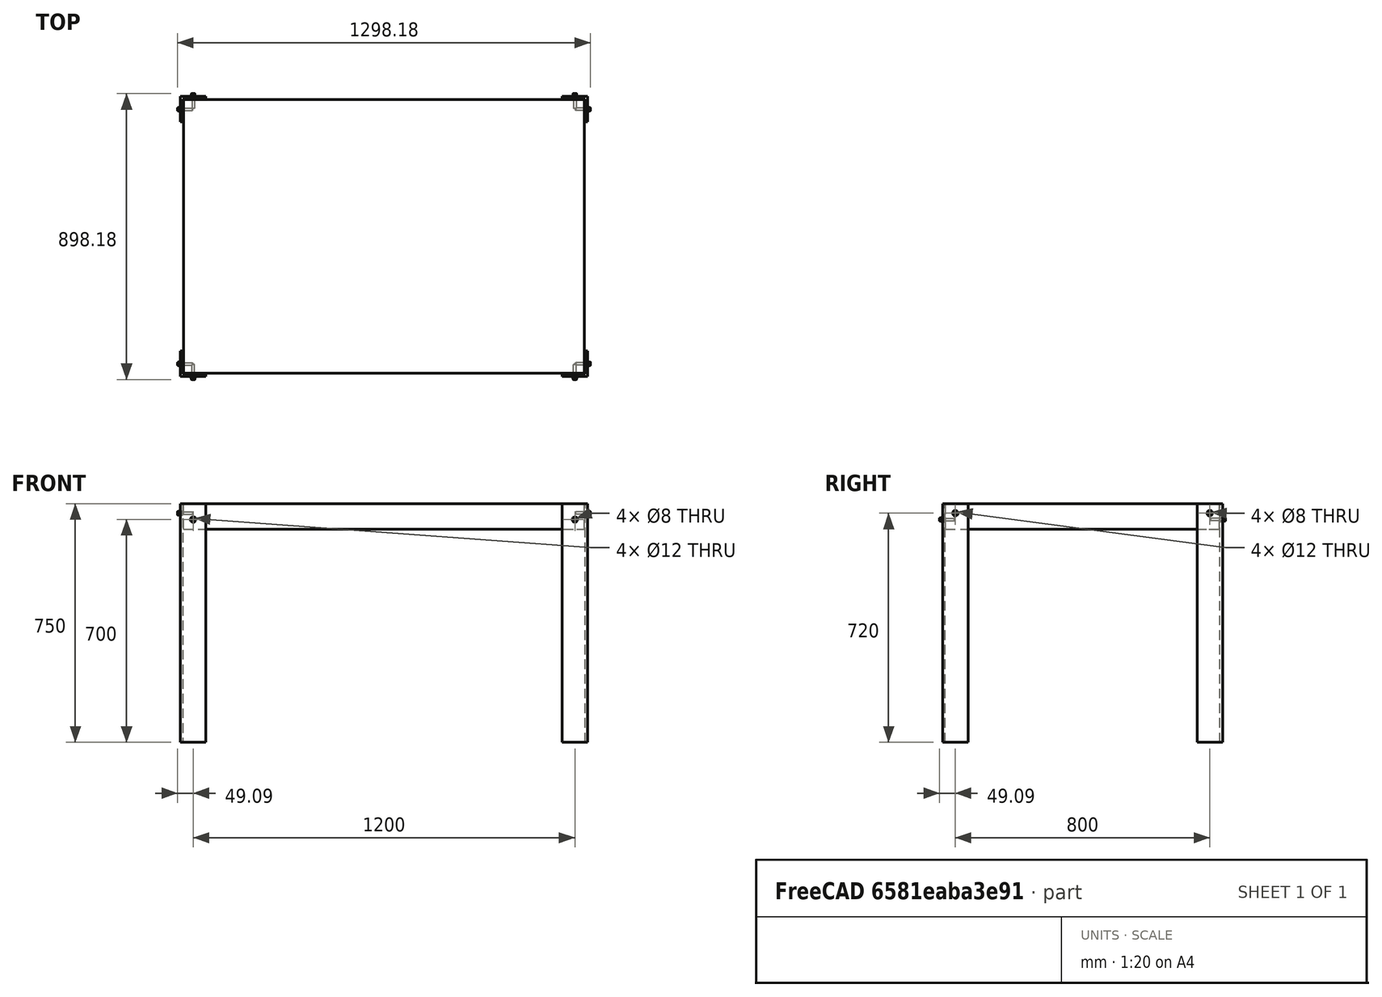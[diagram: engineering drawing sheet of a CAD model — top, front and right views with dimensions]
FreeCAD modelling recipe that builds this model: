
FCSTD DOCUMENT  (FreeCAD 0.17R7797 (Git))
Label: render
License: CreativeCommons Attribution
LicenseURL: http://creativecommons.org/licenses/by/4.0/
objects: Raytracing::RayFeature×13, Raytracing::LuxFeature×13, Part::Cut×12, Part::Box×9, Part::FeaturePython×8, Part::Cylinder×4, App::DocumentObjectGroup×1, Raytracing::RayProject×1, Raytracing::LuxProject×1
note: 33 computed .brp shape members not serialized (recipe doc carries the construction recipe); baked Part::Feature solids carry a one-line shape summary decoded from their .brp

FEATURE [Part::Box] Box  label="Cube"
  AttacherType = Attacher::AttachEngine3D
  Height = 750
  Length = 80
  Width = 80
FEATURE [Part::Box] Box001  label="Cube001"
  AttacherType = Attacher::AttachEngine3D
  Height = 750
  Length = 80
  Placement = pos=(8,8,0) rot=(0,0,1;0rad)
  Width = 80
FEATURE [Part::Cut] Cut
  Base = -> Box
  Tool = -> Box001
FEATURE [Part::Box] Box002  label="Cube002"
  AttacherType = Attacher::AttachEngine3D
  Height = 750
  Length = 80
  Placement = pos=(0,800,0) rot=(0,0,1;0rad)
  Width = 80
FEATURE [Part::Box] Box003  label="Cube003"
  AttacherType = Attacher::AttachEngine3D
  Height = 750
  Length = 80
  Placement = pos=(8,792,0) rot=(0,0,1;0rad)
  Width = 80
FEATURE [Part::Cut] Cut001
  Base = -> Box002
  Tool = -> Box003
FEATURE [Part::Box] Box004  label="Cube004"
  AttacherType = Attacher::AttachEngine3D
  Height = 750
  Length = 80
  Placement = pos=(1200,0,0) rot=(0,0,1;0rad)
  Width = 80
FEATURE [Part::Box] Box005  label="Cube005"
  AttacherType = Attacher::AttachEngine3D
  Height = 750
  Length = 80
  Placement = pos=(1192,8,0) rot=(0,0,1;0rad)
  Width = 80
FEATURE [Part::Cut] Cut002
  Base = -> Box004
  Tool = -> Box005
FEATURE [Part::Box] Box006  label="Cube006"
  AttacherType = Attacher::AttachEngine3D
  Height = 750
  Length = 80
  Placement = pos=(1200,800,0) rot=(0,0,1;0rad)
  Width = 80
FEATURE [Part::Box] Box007  label="Cube007"
  AttacherType = Attacher::AttachEngine3D
  Height = 750
  Length = 80
  Placement = pos=(1192,792,0) rot=(0,0,1;0rad)
  Width = 80
FEATURE [Part::Cut] Cut003
  Base = -> Box006
  Tool = -> Box007
FEATURE [Part::Box] Box008  label="Tabletop"
  AttacherType = Attacher::AttachEngine3D
  Height = 80
  Length = 1260
  Placement = pos=(10,10,670) rot=(0,0,1;0rad)
  Width = 860
  expr: Width = 880 - 20
  expr: Length = 1280 - 20
FEATURE [Part::Cylinder] Cylinder
  Angle = 360
  AttacherType = Attacher::AttachEngine3D
  Height = 1300
  Placement = pos=(-10,40,720) rot=(0,1,0;1.5708rad)
  Radius = 6
FEATURE [Part::Cylinder] Cylinder001
  Angle = 360
  AttacherType = Attacher::AttachEngine3D
  Height = 1300
  Placement = pos=(-10,840,720) rot=(0,1,0;1.5708rad)
  Radius = 6
FEATURE [Part::Cylinder] Cylinder002
  Angle = 360
  AttacherType = Attacher::AttachEngine3D
  Height = 900
  Placement = pos=(40,-10,700) rot=(-1,0,0;1.5708rad)
  Radius = 6
FEATURE [Part::Cylinder] Cylinder003
  Angle = 360
  AttacherType = Attacher::AttachEngine3D
  Height = 900
  Placement = pos=(1240,-10,700) rot=(-1,0,0;1.5708rad)
  Radius = 6
FEATURE [Part::Cut] Cut004
  Base = -> Cut
  Tool = -> Cylinder
FEATURE [Part::Cut] Cut005
  Base = -> Cut002
  Tool = -> Cylinder
FEATURE [Part::Cut] Cut006  label="Foot 01"
  Base = -> Cut004
  Tool = -> Cylinder002
FEATURE [Part::Cut] Cut007
  Base = -> Cut001
  Tool = -> Cylinder002
FEATURE [Part::Cut] Cut008  label="Foot 02"
  Base = -> Cut007
  Tool = -> Cylinder001
FEATURE [Part::Cut] Cut009
  Base = -> Cut003
  Tool = -> Cylinder001
FEATURE [Part::Cut] Cut010  label="Foot 03"
  Base = -> Cut009
  Tool = -> Cylinder003
FEATURE [Part::Cut] Cut011  label="Foot 04"
  Base = -> Cut005
  Tool = -> Cylinder003
FEATURE [Part::FeaturePython] Screw  label="M8x40-Screw"  # Fasteners workbench fastener (typed FeaturePython)
  Placement = pos=(-2,40,720) rot=(0,-1,0;1.5708rad)
  diameter = 3
  invert = false
  length = 5
  matchOuter = false
  offset = 0
  thread = false
  type = 1
FEATURE [Part::FeaturePython] Screw001  label="M8x40-Screw001"  # Fasteners workbench fastener (typed FeaturePython)
  Placement = pos=(-2,840,720) rot=(0,-1,0;1.5708rad)
  diameter = 3
  invert = false
  length = 5
  matchOuter = false
  offset = 0
  thread = false
  type = 1
FEATURE [Part::FeaturePython] Screw002  label="M8x40-Screw002"  # Fasteners workbench fastener (typed FeaturePython)
  Placement = pos=(1282,40,720) rot=(0,1,0;1.5708rad)
  diameter = 3
  invert = false
  length = 5
  matchOuter = false
  offset = 0
  thread = false
  type = 1
FEATURE [Part::FeaturePython] Screw003  label="M8x40-Screw003"  # Fasteners workbench fastener (typed FeaturePython)
  Placement = pos=(1282,840,720) rot=(0,1,0;1.5708rad)
  diameter = 3
  invert = false
  length = 5
  matchOuter = false
  offset = 0
  thread = false
  type = 1
FEATURE [Part::FeaturePython] Screw004  label="M8x40-Screw007"  # Fasteners workbench fastener (typed FeaturePython)
  Placement = pos=(40,882,700) rot=(-1,0,0;1.5708rad)
  diameter = 3
  invert = false
  length = 5
  matchOuter = false
  offset = 0
  thread = false
  type = 1
FEATURE [Part::FeaturePython] Screw005  label="M8x40-Screw005"  # Fasteners workbench fastener (typed FeaturePython)
  Placement = pos=(1240,-2,700) rot=(1,0,0;1.5708rad)
  diameter = 3
  invert = false
  length = 5
  matchOuter = false
  offset = 0
  thread = false
  type = 1
FEATURE [Part::FeaturePython] Screw006  label="M8x40-Screw006"  # Fasteners workbench fastener (typed FeaturePython)
  Placement = pos=(40,-2,700) rot=(1,0,0;1.5708rad)
  diameter = 3
  invert = false
  length = 5
  matchOuter = false
  offset = 0
  thread = false
  type = 1
FEATURE [Part::FeaturePython] Screw007  label="M8x40-Screw008"  # Fasteners workbench fastener (typed FeaturePython)
  Placement = pos=(1240,882,700) rot=(-1,0,0;1.5708rad)
  diameter = 3
  invert = false
  length = 5
  matchOuter = false
  offset = 0
  thread = false
  type = 1
FEATURE [App::DocumentObjectGroup] Group  label="Screws"
  Group = -> [Screw,Screw001,Screw002,Screw003,Screw004,Screw005,Screw006,Screw007]
FEATURE [Raytracing::RayFeature] Cut006_View
  Result = <blob: 18464 chars omitted>
  Source = -> Cut006
  Transparency = 0
FEATURE [Raytracing::RayFeature] Cut008_View
  Result = <blob: 18274 chars omitted>
  Source = -> Cut008
  Transparency = 0
FEATURE [Raytracing::RayFeature] Cut010_View
  Result = <blob: 18288 chars omitted>
  Source = -> Cut010
  Transparency = 0
FEATURE [Raytracing::RayFeature] Cut011_View
  Result = <blob: 18398 chars omitted>
  Source = -> Cut011
  Transparency = 0
FEATURE [Raytracing::RayFeature] Box008_View
  Result = <blob: 2757 chars omitted>
  Source = -> Box008
  Transparency = 0
FEATURE [Raytracing::RayFeature] Screw_View
  Result = <blob: 147194 chars omitted>
  Source = -> Screw
  Transparency = 0
FEATURE [Raytracing::RayFeature] Screw001_View
  Result = <blob: 147808 chars omitted>
  Source = -> Screw001
  Transparency = 0
FEATURE [Raytracing::RayFeature] Screw002_View
  Result = <blob: 146709 chars omitted>
  Source = -> Screw002
  Transparency = 0
FEATURE [Raytracing::RayFeature] Screw003_View
  Result = <blob: 147088 chars omitted>
  Source = -> Screw003
  Transparency = 0
FEATURE [Raytracing::RayFeature] Screw004_View
  Result = <blob: 147220 chars omitted>
  Source = -> Screw004
  Transparency = 0
FEATURE [Raytracing::RayFeature] Screw005_View
  Result = <blob: 148196 chars omitted>
  Source = -> Screw005
  Transparency = 0
FEATURE [Raytracing::RayFeature] Screw006_View
  Result = <blob: 148226 chars omitted>
  Source = -> Screw006
  Transparency = 0
FEATURE [Raytracing::RayFeature] Screw007_View
  Result = <blob: 147459 chars omitted>
  Source = -> Screw007
  Transparency = 0
FEATURE [Raytracing::RayProject] PovProject
  Camera = // declares positon and view direction\n\n// Generated by FreeCAD (http://www.freecadweb.org/)\n#declare cam_location =  <-758.379,1255.67,-1408.27>;\n#declare cam_look_at  = <524.66,496.986,49.8524>;\n#declare cam_sky      = <0.254713,0.931287,0.260434>;\n#declare cam_angle    = 45; \ncamera {\n  location  cam_location\n  look_at   cam_look_at\n  sky       cam_sky\n  angle     cam_angle \n  right x*1920/1080\n}
  Group = -> [Cut006_View,Cut008_View,Cut010_View,Cut011_View,Box008_View,Screw_View,Screw001_View,Screw002_View,Screw003_View,Screw004_View,Screw005_View,Screw006_View,Screw007_View]
  Template = <userpath>/Apps/FreeCAD/data/Mod/Raytracing/Templates/RadiosityNormal.pov
FEATURE [Raytracing::LuxFeature] Box008_View001
  Result = MakeNamedMaterial "FreeCADMaterial_Lux_Box008"\n    "color Kd" [0.580392 0.439216 0.360784]\n    "float sigma" [0.000000000000000]\n    "string type" ["matte"]\n\nAttributeBegin #  "Lux_Box008"\nTransform [1 0 0 0 0 1 0 0 0 0 1 0 0 0 0 1]\nNamedMaterial "FreeCADMaterial_Lux_Box008"\nShape "mesh"\n    "integer triindices" [3 2 1 0 3 1 5 6 7 5 7 4 9 8 10 8 11 10 14 12 13 14 15 12 17 16 18 16 19 18 22 20 21 22 23 20 ]\n    "point P" [10 10 670 10 10 750 10 870 750 10 870 670 1270 10 670 1270 10 750 1270 870 750 1270 870 670 10 10 670 1270 10 670 1270 10 750 10 10 750 10 870 670 1270 870 670 1270 870 750 10 870 750 10 10 670 10 870 670 1270 870 670 1270 10 670 10 10 750 10 870 750 1270 870 750 1270 10 750 ]\n    "normal N" [-1 -0 0 -1 -0 0 -1 -0 0 -1 -0 0 1 0 -0 1 0 -0 1 0 -0 1 0 -0 -0 -1 -0 -0 -1 -0 -0 -1 -0 -0 -1 -0 0 1 0 0 1 0 0 1 0 0 1 0 -0 -0 -1 -0 -0 -1 -0 -0 -1 -0 -0 -1 0 0 1 0 0 1 0 0 1 0 0 1 ]\n    "bool generatetangents" ["false"]\n    "string name" ["Lux_Box008"]\nAttributeEnd # ""
  Source = -> Box008
  Transparency = 0
FEATURE [Raytracing::LuxFeature] Cut006_View001
  Result = <blob: 11779 chars omitted>
  Source = -> Cut006
  Transparency = 0
FEATURE [Raytracing::LuxFeature] Cut008_View001
  Result = <blob: 11589 chars omitted>
  Source = -> Cut008
  Transparency = 0
FEATURE [Raytracing::LuxFeature] Cut010_View001
  Result = <blob: 11627 chars omitted>
  Source = -> Cut010
  Transparency = 0
FEATURE [Raytracing::LuxFeature] Cut011_View001
  Result = <blob: 11736 chars omitted>
  Source = -> Cut011
  Transparency = 0
FEATURE [Raytracing::LuxFeature] Screw_View001
  Result = <blob: 109134 chars omitted>
  Source = -> Screw
  Transparency = 0
FEATURE [Raytracing::LuxFeature] Screw001_View001
  Result = <blob: 109552 chars omitted>
  Source = -> Screw001
  Transparency = 0
FEATURE [Raytracing::LuxFeature] Screw002_View001
  Result = <blob: 108520 chars omitted>
  Source = -> Screw002
  Transparency = 0
FEATURE [Raytracing::LuxFeature] Screw003_View001
  Result = <blob: 108833 chars omitted>
  Source = -> Screw003
  Transparency = 0
FEATURE [Raytracing::LuxFeature] Screw004_View001
  Result = <blob: 109015 chars omitted>
  Source = -> Screw004
  Transparency = 0
FEATURE [Raytracing::LuxFeature] Screw005_View001
  Result = <blob: 110010 chars omitted>
  Source = -> Screw005
  Transparency = 0
FEATURE [Raytracing::LuxFeature] Screw006_View001
  Result = <blob: 110019 chars omitted>
  Source = -> Screw006
  Transparency = 0
FEATURE [Raytracing::LuxFeature] Screw007_View001
  Result = <blob: 109206 chars omitted>
  Source = -> Screw007
  Transparency = 0
FEATURE [Raytracing::LuxProject] LuxProject
  Camera = # declares positon and view direction\n# Generated by FreeCAD (http://www.freecadweb.org/)\nLookAt -1002.12 -1649.12 1374.75 281.983 -222.546 559.959 0.275799 0.277386 0.920322
  Group = -> [Box008_View001,Cut006_View001,Cut008_View001,Cut010_View001,Cut011_View001,Screw_View001,Screw001_View001,Screw002_View001,Screw003_View001,Screw004_View001,Screw005_View001,Screw006_View001,Screw007_View001]
  Template = <userpath>/Apps/FreeCAD/data/Mod/Raytracing/Templates/LuxOutdoor.lxs
